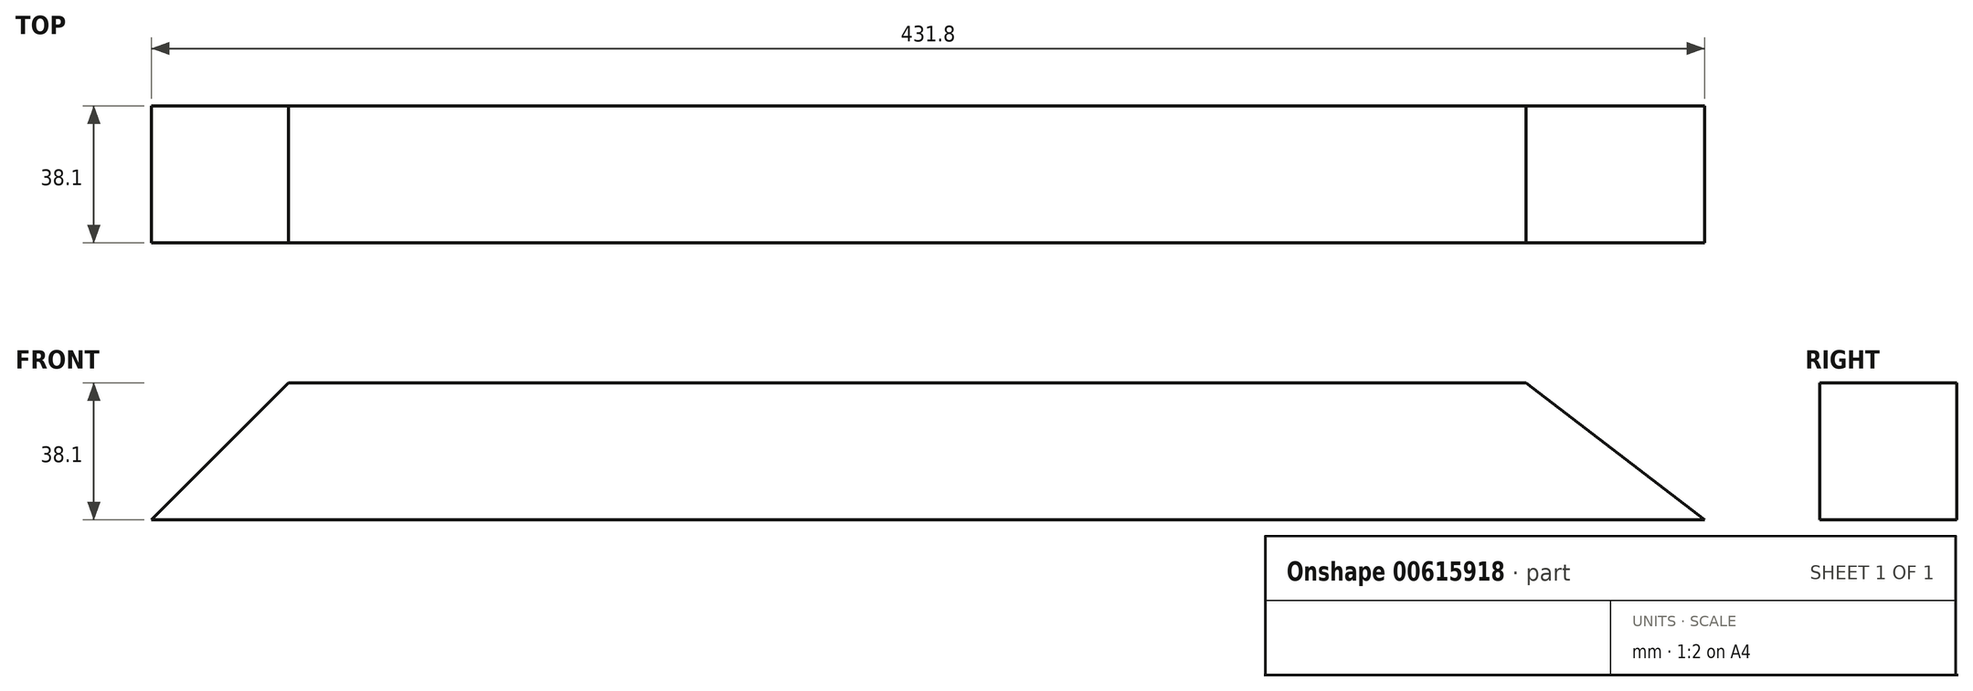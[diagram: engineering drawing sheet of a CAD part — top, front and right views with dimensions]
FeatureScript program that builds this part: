
annotation { "Feature Type Name" : "Feature", "Feature Type Description" : "" }
export const myFeature = defineFeature(function(context is Context, id is Id, definition is map)
    precondition{}
    {
        {
            var Q0;
            Q0=qCreatedBy(makeId("Front.planeOp"),FACE);
            var sketch = newSketch(context, id + "F0", { "sketchPlane" : qUnion([Q0])});
            skLineSegment(sketch, "E0.top", {"start": v(-215.9, -19.05) * mm, "end": v(215.9, -19.05) * mm});
            skLineSegment(sketch, "E0.left", {"start": v(-215.9, 19.05) * mm, "end": v(-215.9, -19.05) * mm});
            skPoint(sketch, "E0.middle", {"position": v(0, 0) * mm});
            skLineSegment(sketch, "E1", {"start": v(215.9, -19.05) * mm, "end": v(166.25, 19.05) * mm});
            skLineSegment(sketch, "E2", {"start": v(-215.9, 19.05) * mm, "end": v(166.25, 19.05) * mm});
            skSolve(sketch);
        }
        {
            var Q0;
            Q0 = qSketchRegion(id + "F0", true);
            extrude(context, id + "F1", {"entities" : qUnion([Q0]), "endBound" : BoundingType.SYMMETRIC, "depth" : 38.1 * mm, "offsetDistance" : 25.4 * mm});
        }
        {
            var Q0;
            Q0=makeQuery(id+"F1.opExtrude","SWEPT_EDGE",EDGE,{"disambiguationData":[OSD([sQuery(id+"F0.wireOp",EDGE,"E0.left"),sQuery(id+"F0.wireOp",EDGE,"E2")])]});
            chamfer(context, id + "F2", {"entities" : qUnion([Q0]), "width" : 38.1 * mm, "tangentPropagation" : true});
        }
    });
